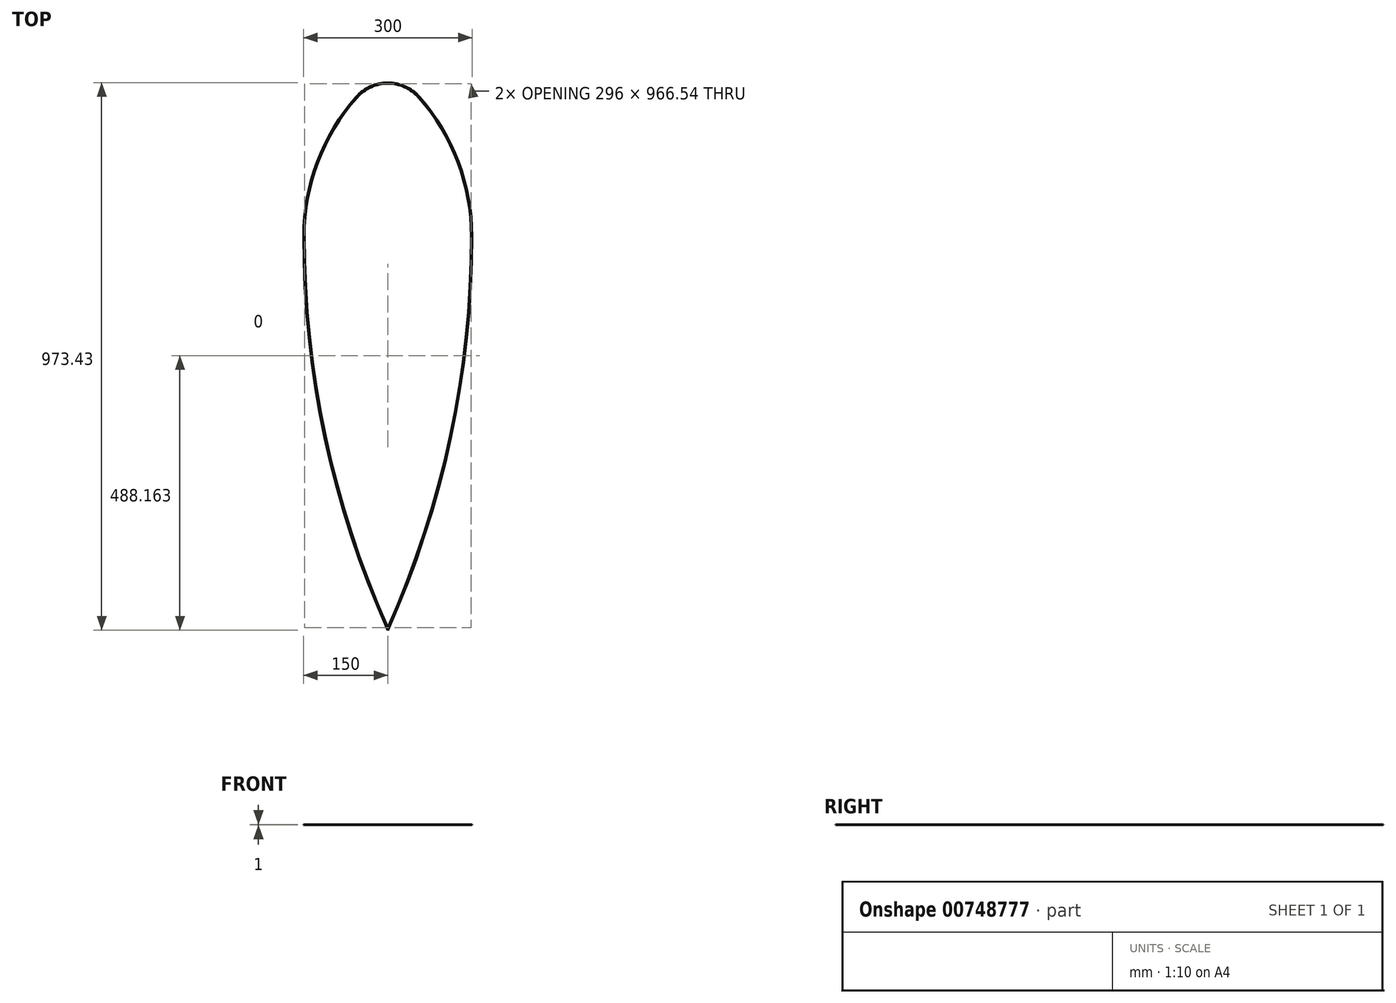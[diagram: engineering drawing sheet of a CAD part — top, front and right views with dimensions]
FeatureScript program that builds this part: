
annotation { "Feature Type Name" : "Feature", "Feature Type Description" : "" }
export const myFeature = defineFeature(function(context is Context, id is Id, definition is map)
    precondition{}
    {
        {
            var Q0;
            Q0=qCreatedBy(makeId("Top.planeOp"),FACE);
            var sketch = newSketch(context, id + "F0", { "sketchPlane" : qUnion([Q0])});
            skLineSegment(sketch, "E0.bottom", {"start": v(150, 300) * mm, "end": v(-150, 300) * mm, "construction": true});
            skLineSegment(sketch, "E0.top", {"start": v(150, -700) * mm, "end": v(-150, -700) * mm, "construction": true});
            skLineSegment(sketch, "E0.left", {"start": v(150, 300) * mm, "end": v(150, -700) * mm});
            skLineSegment(sketch, "E0.right", {"start": v(-150, 300) * mm, "end": v(-150, -700) * mm, "construction": true});
            skPoint(sketch, "E0.middle", {"position": v(0, -200) * mm});
            skLineSegment(sketch, "E1", {"start": v(0, 300) * mm, "end": v(0, -700) * mm, "construction": true});
            skPoint(sketch, "E2.orphan", {"position": v(0, 300) * mm});
            skArc(sketch, "E3", {"start": v(-56.25, 248.04) * mm, "mid": v(-125.78, 132.58) * mm, "end": v(-150, 0) * mm});
            skArc(sketch, "E4.MirrorCS", {"start": v(150, 0) * mm, "mid": v(112.08, -357.95) * mm, "end": v(0, -700) * mm});
            skArc(sketch, "E5.MirrorCS", {"start": v(56.25, 248.04) * mm, "mid": v(125.78, 132.58) * mm, "end": v(150, 0) * mm});
            skArc(sketch, "E6.trimOffspring", {"start": v(-150, 0) * mm, "mid": v(-112.08, -357.95) * mm, "end": v(0, -700) * mm});
            skLineSegment(sketch, "E7", {"start": v(0, 0) * mm, "end": v(-1558.33, 0) * mm, "construction": true});
            skLineSegment(sketch, "E8", {"start": v(0, 0) * mm, "end": v(1558.33, 0) * mm, "construction": true});
            skArc(sketch, "E9.filletArc", {"start": v(56.25, 248.04) * mm, "mid": v(0, 273.43) * mm, "end": v(-56.25, 248.04) * mm});
            skArc(sketch, "E10.0", {"start": v(148, 0) * mm, "mid": v(110.59, -355.34) * mm, "end": v(0, -695.1) * mm});
            skArc(sketch, "E10.1", {"start": v(54.75, 246.72) * mm, "mid": v(123.9, 131.88) * mm, "end": v(148, 0) * mm});
            skArc(sketch, "E10.2", {"start": v(-148, 0) * mm, "mid": v(-110.59, -355.34) * mm, "end": v(0, -695.1) * mm});
            skArc(sketch, "E10.3", {"start": v(-54.75, 246.72) * mm, "mid": v(-123.9, 131.88) * mm, "end": v(-148, 0) * mm});
            skArc(sketch, "E10.4", {"start": v(54.75, 246.72) * mm, "mid": v(0, 271.43) * mm, "end": v(-54.75, 246.72) * mm});
            skSolve(sketch);
        }
        {
            var Q0;
            Q0=makeQuery(id+"F0.imprint","IMPRINT",FACE,{"disambiguationData":[TD([[makeQuery(id+"F0.imprint","IMPRINT",EDGE,{"derivedFrom":sQuery(id+"F0.wireOp",EDGE,"E10.0")}),-1.0]])]});
            extrude(context, id + "F1", {"entities" : qUnion([Q0]), "depth" : 1 * mm, "offsetDistance" : 25 * mm});
        }
    });
